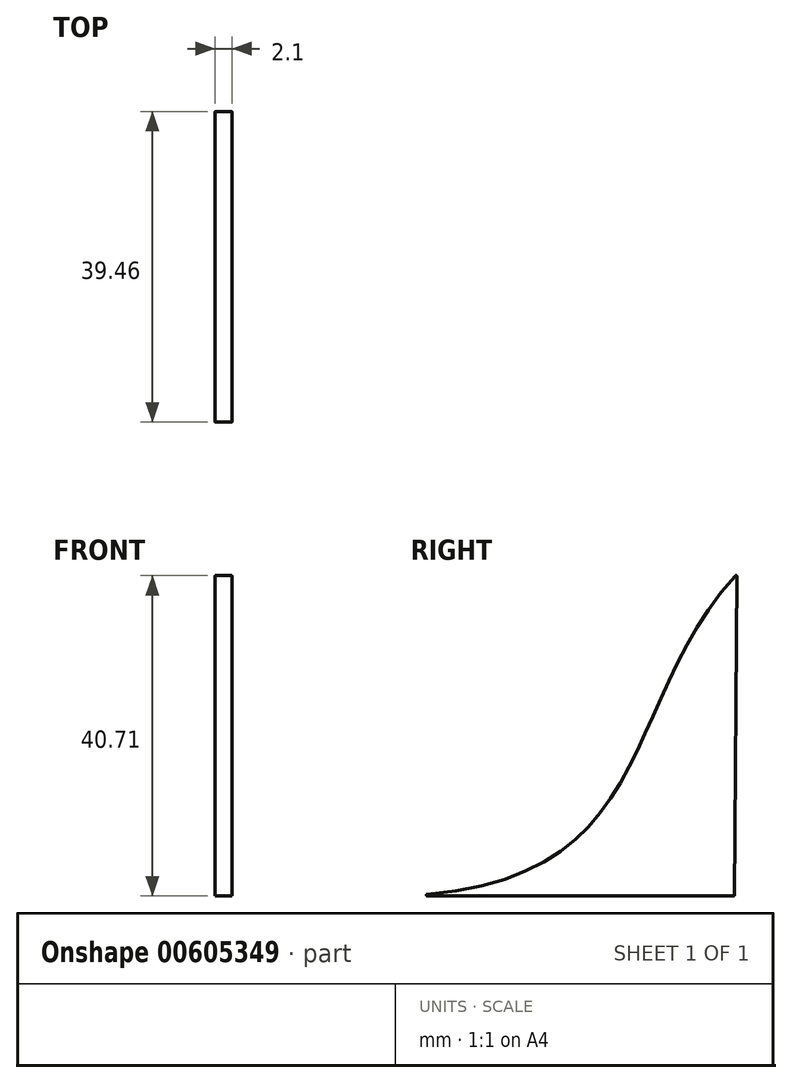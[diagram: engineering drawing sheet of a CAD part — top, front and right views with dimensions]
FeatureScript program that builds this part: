
annotation { "Feature Type Name" : "Feature", "Feature Type Description" : "" }
export const myFeature = defineFeature(function(context is Context, id is Id, definition is map)
    precondition{}
    {
        {
            var Q0;
            Q0=qCreatedBy(makeId("Right.planeOp"),FACE);
            var sketch = newSketch(context, id + "F0", { "sketchPlane" : qUnion([Q0])});
            skLineSegment(sketch, "E0", {"start": v(-22.5, 0) * mm, "end": v(22.5, 0) * mm});
            skFitSpline(sketch, "E1", {"points": [v(-22.5, 0) * mm, v(22.8, 40.9) * mm], "startDerivative": vector(108.68, 0) * mm, "endDerivative": vector(47.65, 51.46) * mm});
            skLineSegment(sketch, "E2", {"start": v(22.8, 40.9) * mm, "end": v(22.5, 0) * mm});
            skSolve(sketch);
        }
        {
            var Q0;
            Q0=makeQuery(id+"F0.imprint","IMPRINT",FACE,{"disambiguationData":[TD([[makeQuery(id+"F0.imprint","IMPRINT",EDGE,{"derivedFrom":sQuery(id+"F0.wireOp",EDGE,"E0")}),1.0]])]});
            extrude(context, id + "F1", {"entities" : qUnion([Q0]), "depth" : 2.1 * mm, "offsetDistance" : 25 * mm});
        }
        {
            var Q0;
            Q0=makeQuery(id+"F1.opExtrude","SWEPT_EDGE",EDGE,{"disambiguationData":[OSD([sQuery(id+"F0.wireOp",EDGE,"E1"),sQuery(id+"F0.wireOp",EDGE,"E2")])]});
            var Q1;
            Q1=makeQuery(id+"F1.opExtrude","SWEPT_EDGE",EDGE,{"disambiguationData":[OSD([sQuery(id+"F0.wireOp",EDGE,"E0"),sQuery(id+"F0.wireOp",EDGE,"E2")])]});
            var Q2;
            Q2=makeQuery(id+"F1.opExtrude","SWEPT_EDGE",EDGE,{"disambiguationData":[OSD([sQuery(id+"F0.wireOp",EDGE,"E0"),sQuery(id+"F0.wireOp",EDGE,"E1")])]});
            fillet(context, id + "F2", {"entities" : qUnion([Q0, Q1, Q2]), "radius" : 0.12 * mm, "tangentPropagation" : true, "allowEdgeOverflow" : false});
        }
    });
